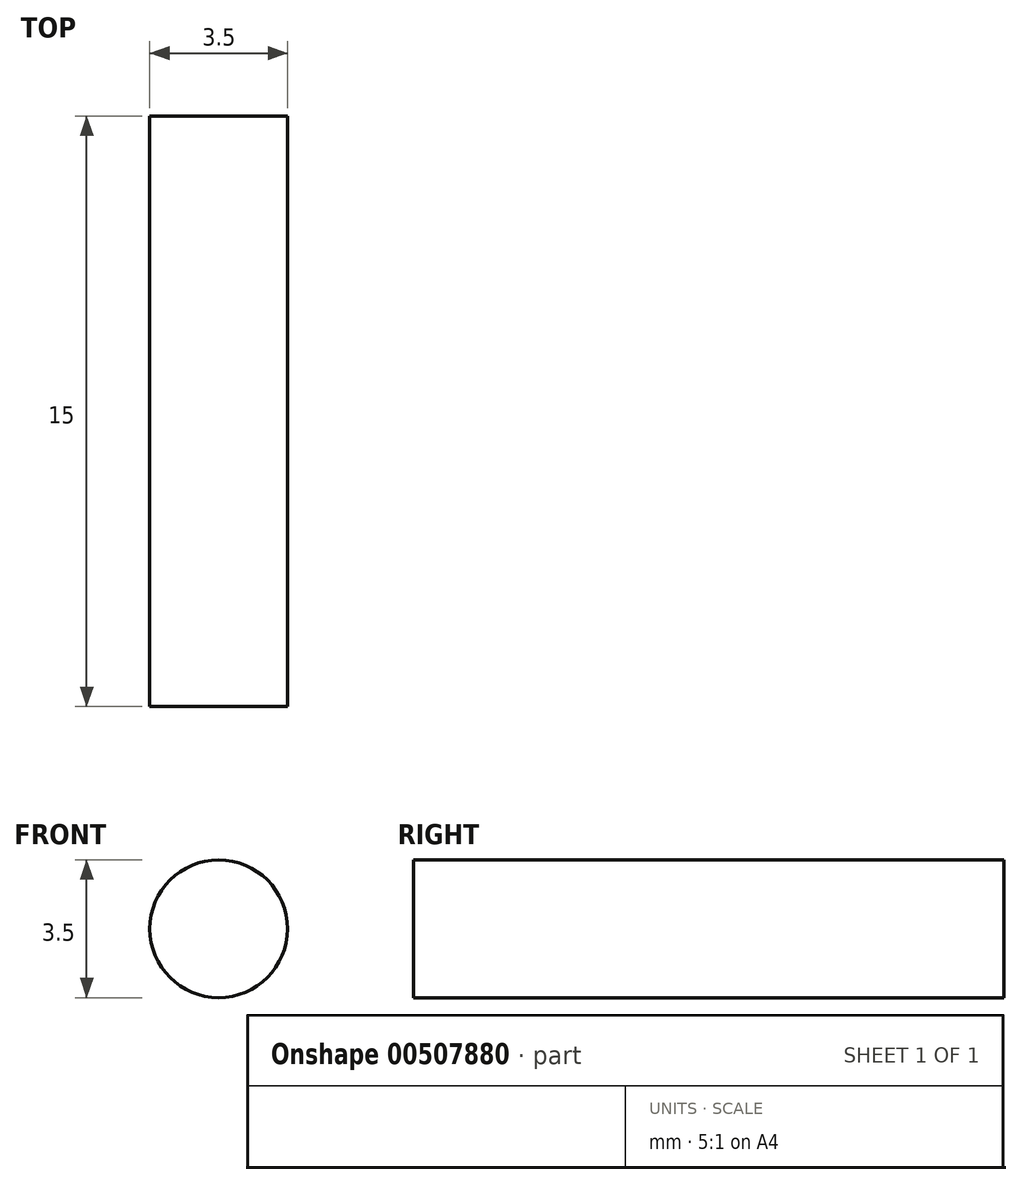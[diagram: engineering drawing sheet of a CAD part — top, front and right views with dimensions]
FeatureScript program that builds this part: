
annotation { "Feature Type Name" : "Feature", "Feature Type Description" : "" }
export const myFeature = defineFeature(function(context is Context, id is Id, definition is map)
    precondition{}
    {
        {
            var Q0;
            Q0=qCreatedBy(makeId("Front.planeOp"),FACE);
            var sketch = newSketch(context, id + "F0", { "sketchPlane" : qUnion([Q0])});
            skCircle(sketch, "E0", {"center": v(0, 0) * mm, "radius": 1.75 * mm});
            skSolve(sketch);
        }
        {
            var Q0;
            Q0=makeQuery(id+"F0.imprint","IMPRINT",FACE,{"disambiguationData":[TD([[makeQuery(id+"F0.imprint","IMPRINT",EDGE,{"derivedFrom":sQuery(id+"F0.wireOp",EDGE,"E0")}),1.0]])]});
            var Q1;
            Q1=sQuery(id+"F0.wireOp",EDGE,"E0");
            extrude(context, id + "F1", {"entities" : qUnion([Q0]), "surfaceEntities" : qUnion([Q1]), "depth" : 15 * mm, "offsetDistance" : 25 * mm, "symmetric" : true});
        }
    });
